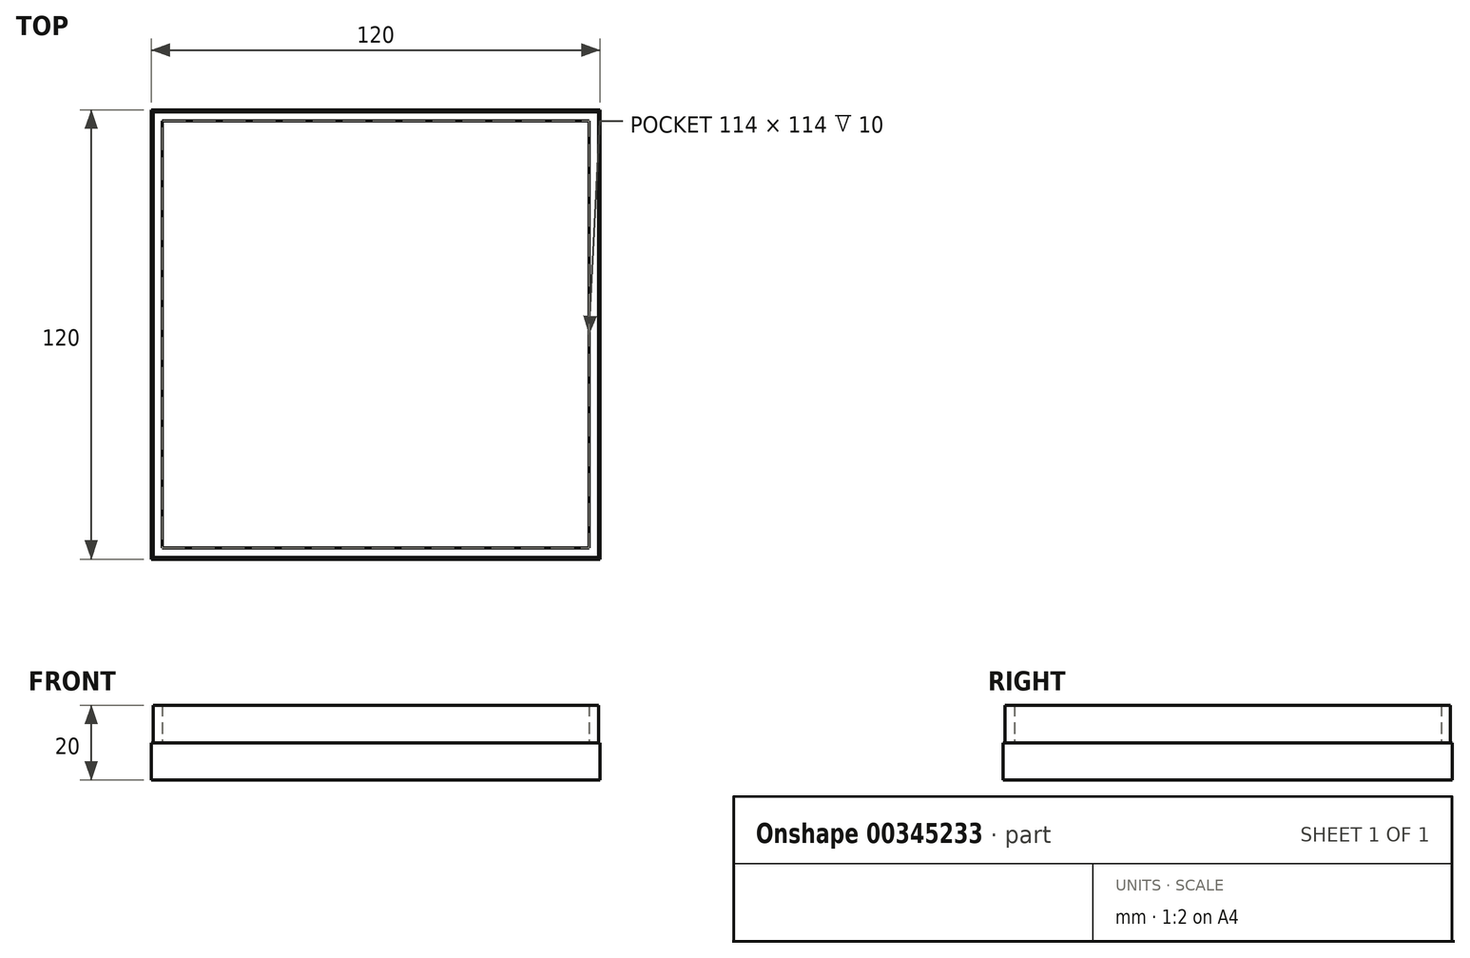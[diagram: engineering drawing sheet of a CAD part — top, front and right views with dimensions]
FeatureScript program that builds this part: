
annotation { "Feature Type Name" : "Feature", "Feature Type Description" : "" }
export const myFeature = defineFeature(function(context is Context, id is Id, definition is map)
    precondition{}
    {
        {
            var Q0;
            Q0=qCreatedBy(makeId("Top.planeOp"),FACE);
            var sketch = newSketch(context, id + "F0", { "sketchPlane" : qUnion([Q0])});
            skLineSegment(sketch, "E0.bottom", {"start": v(-60, 60) * mm, "end": v(60, 60) * mm});
            skLineSegment(sketch, "E0.top", {"start": v(-60, -60) * mm, "end": v(60, -60) * mm});
            skLineSegment(sketch, "E0.left", {"start": v(-60, 60) * mm, "end": v(-60, -60) * mm});
            skLineSegment(sketch, "E0.right", {"start": v(60, 60) * mm, "end": v(60, -60) * mm});
            skPoint(sketch, "E0.middle", {"position": v(0, 0) * mm});
            skSolve(sketch);
        }
        {
            var Q0;
            Q0=makeQuery(id+"F0.imprint","IMPRINT",FACE,{"disambiguationData":[TD([[makeQuery(id+"F0.imprint","IMPRINT",EDGE,{"derivedFrom":sQuery(id+"F0.wireOp",EDGE,"E0.bottom")}),-1.0]])]});
            extrude(context, id + "F1", {"entities" : qUnion([Q0]), "depth" : 10 * mm});
        }
        {
            var Q0;
            Q0=makeQuery(id+"F1.opExtrude","CAP_FACE",FACE,{"disambiguationData":[OSD([sQuery(id+"F0.wireOp",EDGE,"E0.bottom"),sQuery(id+"F0.wireOp",EDGE,"E0.top"),sQuery(id+"F0.wireOp",EDGE,"E0.left"),sQuery(id+"F0.wireOp",EDGE,"E0.right")])],"isStart":false});
            var sketch = newSketch(context, id + "F2", { "sketchPlane" : qUnion([Q0])});
            skLineSegment(sketch, "E1.bottom", {"start": v(-57, 57) * mm, "end": v(57, 57) * mm});
            skLineSegment(sketch, "E1.top", {"start": v(-57, -57) * mm, "end": v(57, -57) * mm});
            skLineSegment(sketch, "E1.left", {"start": v(-57, 57) * mm, "end": v(-57, -57) * mm});
            skLineSegment(sketch, "E1.right", {"start": v(57, 57) * mm, "end": v(57, -57) * mm});
            skPoint(sketch, "E1.middle", {"position": v(0, 0) * mm});
            skLineSegment(sketch, "E2.bottom", {"start": v(-59.5, 59.5) * mm, "end": v(59.5, 59.5) * mm});
            skLineSegment(sketch, "E2.top", {"start": v(-59.5, -59.5) * mm, "end": v(59.5, -59.5) * mm});
            skLineSegment(sketch, "E2.left", {"start": v(-59.5, 59.5) * mm, "end": v(-59.5, -59.5) * mm});
            skLineSegment(sketch, "E2.right", {"start": v(59.5, 59.5) * mm, "end": v(59.5, -59.5) * mm});
            skSolve(sketch);
        }
        {
            var Q0;
            Q0=qSketchRegion(id+"F2",true);
            extrude(context, id + "F3", {"entities" : qUnion([Q0]), "operationType" : NewBodyOperationType.ADD, "depth" : 10 * mm});
        }
    });
